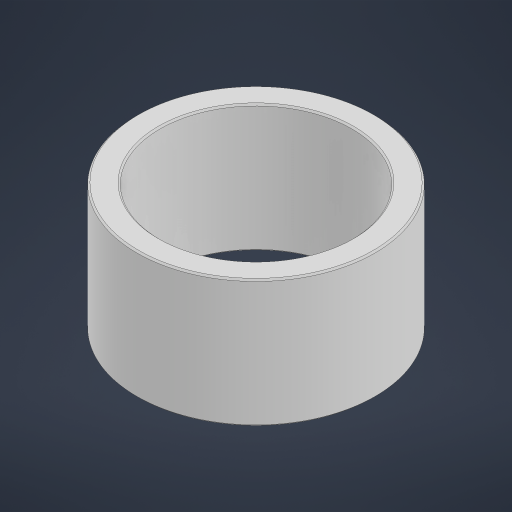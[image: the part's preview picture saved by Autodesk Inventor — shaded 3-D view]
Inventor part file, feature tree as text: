
AUTODESK INVENTOR PART (.ipt)
format: ipt  version: 2023 (Build 270158000, 158)  size: 175,104 bytes
history: native  units: in
note: dims shown in document units (in); Inventor stores cm internally (conversion verified against a paired STEP export)
features: chamfer x1
ambient origin geometry x8: Origin, YZ Plane, XZ Plane, XY Plane, X Axis, Y Axis, Z Axis, Center Point
bodies: Solid1 (feature_tree)
feature tree (1):
  chamfer  "Chamfer1"  [1 undecoded]
note: 1 required parameter value undecoded (feature->parameter linkage not recoverable at this tier; creation-order binding heuristic only, values carry confidence <= 0.55)
